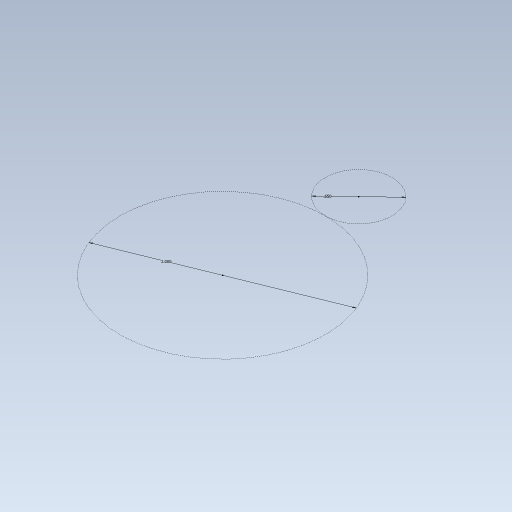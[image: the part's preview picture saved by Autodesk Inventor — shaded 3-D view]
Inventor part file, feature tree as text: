
AUTODESK INVENTOR PART (.ipt)
format: ipt  version: 2024 (Build 280153000, 153)  size: 70,144 bytes
history: native  units: in
note: dims shown in document units (in); Inventor stores cm internally (conversion verified against a paired STEP export)
features: sketch x1
ambient origin geometry x8: Origin, YZ Plane, XZ Plane, XY Plane, X Axis, Y Axis, Z Axis, Center Point
feature tree (1):
  sketch  "Sketch1"  dims[d0=2.0in d1=0.65in]
